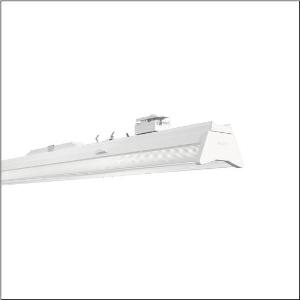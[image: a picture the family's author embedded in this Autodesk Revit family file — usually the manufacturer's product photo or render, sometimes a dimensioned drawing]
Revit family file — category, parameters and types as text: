
# Revit family: licross_r__21_performance_mo_52td16dn46xg_ca4f
name_source: partatom
category: Lighting Fixtures
units: mm (PartAtom-declared; Revit-internal decimal feet)

## family parameters
Cut with Voids When Loaded = No
Host = Face
Light Source = No
Part Type = Normal
Room Calculation Point = No
Round Connector Dimension = Use Diameter
Shared = No

## types (1)
- --- (1 x LED, 6000 lm, 32.7 W, 4000K)
    Apparent Load = 33 VA
    CIE Flux Codes = 66 88 96 79 100
    Color Rendering = 80
    Color Temperature = 4000K
    Default Elevation = 1800 mm
    Description = Licross® 21 Performance MO, luminaire insert, of sheet steel, galvanised, coil coated, white, length: 1.500mm, width: 120mm, height: 123mm, LED rated luminous flux: 6.000lm, light colour: 840, control gear: DALI 2, with plug, 5-pole, with phase selection, mains connection: 220..240V, AC, 50/60Hz, rated input power: 33W, halogen-free wiring, primary light control with lens, of plastic, primary optical cover: cover, of PMMA, light emission: direct/indirect distribution, primary light characteristic: symmetric, protection rating (complete): IP54, insulation class (complete): insulation class I (protective earthing), certification: CE, ENEC, VDE, UKCA, protection symbol: D if used in an environment with non-conductive dust loads with corresponding accessories, impact resistance: IK06, permissible ambient temperature for indoor applications: -25..+45°C, corresponds to IFS (International Featured Standards) requirements for safety and quality in the food industry, reducing of maximum allowable ambient temperature of 5°C with ceiling mounting, LABS conformity tested according to VDMA 24364:2018-05, packaging unit: 1 piece
    Height = 114 mm
    Lamp = 1 x LED
    Lamp Light Flux = 6000 lm
    Lamp Power = 32.7 W
    Lamp count = 1
    Length = 1500 mm
    Luminous efficacy = 183 lm/W
    Manufacturer = Siteco
    ModVariant = No
    Model = 52TD16DN46XG
    Mounting Place = Ceiling
    Mounting Type = Pendant
    Number of Poles = 1
    OnlyDefault = Yes
    Power Factor = 1
    Product Name = Licross® 21 Performance MO
    Product group = luminaire insert
    ProductGroupID = 901
    Protection Class = Protection class I
    Protection Degree = IP 54
    RLX_Detail_Level = 1
    RLX_Emergency_Light_Flux = 0 lm
    RLX_Emergency_Type = 0
    RLX_Emergency_Type_DB = No
    RlxData = <blob elided: 33677 chars, md5=93693877>
    Socket = socket
    Standby Power = 0 W
    System Light Flux = 6000 lm
    System Power = 33 W
    Type Comments = factory setting: luminous flux: 100 % | dim-lin: 254 | 222 mA
    Type Image = l_1256138.jpg
    URL = http://relux.com
    VarID = @adj_060799
    Voltage = 0 V
    Weight = 0.00 kg
    Width = 120 mm

## geometry (parser evidence)
native form markers: Blend x4, Sweep x10
no freeform markers — native parametric forms only
